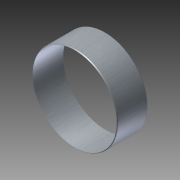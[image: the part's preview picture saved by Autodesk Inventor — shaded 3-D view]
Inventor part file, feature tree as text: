
AUTODESK INVENTOR PART (.ipt)
format: ipt  version: 2011 SP1 (Build 150282100, 282)  size: 97,792 bytes
history: native  units: in
note: dims shown in document units (in); Inventor stores cm internally (conversion verified against a paired STEP export)
features: extrude x1, fillet x1, sketch x1
ambient origin geometry x8: Origin, YZ Plane, XZ Plane, XY Plane, X Axis, Y Axis, Z Axis, Center Point
bodies: Solid1 (feature_tree)
feature tree (3):
  extrude  "Extrusion1"  Depth=8.25in
  fillet  "Fillet1"  Radius=3.0in
  sketch  "Sketch1"  dims[d0=0.0625in d1=8.25in d2=3.0in d3=0.0in d4=0.125in]
